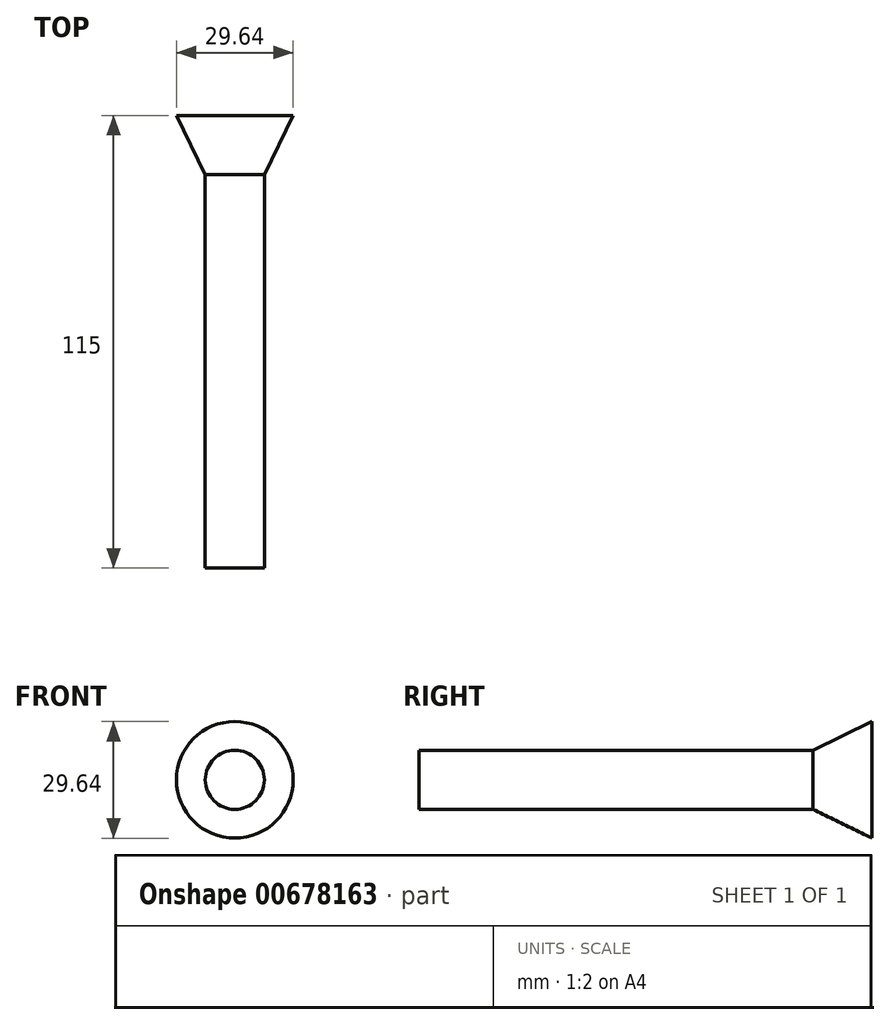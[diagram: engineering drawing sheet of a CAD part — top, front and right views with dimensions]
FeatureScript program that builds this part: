
annotation { "Feature Type Name" : "Feature", "Feature Type Description" : "" }
export const myFeature = defineFeature(function(context is Context, id is Id, definition is map)
    precondition{}
    {
        {
            var Q0;
            Q0=qCreatedBy(makeId("Front.planeOp"),FACE);
            var sketch = newSketch(context, id + "F0", { "sketchPlane" : qUnion([Q0])});
            skCircle(sketch, "E0", {"center": v(0, 0) * mm, "radius": 7.5 * mm});
            skSolve(sketch);
        }
        {
            var Q0;
            Q0=makeQuery(id+"F0.imprint","IMPRINT",FACE,{"disambiguationData":[TD([[makeQuery(id+"F0.imprint","IMPRINT",EDGE,{"derivedFrom":sQuery(id+"F0.wireOp",EDGE,"E0")}),1.0]])]});
            extrude(context, id + "F1", {"entities" : qUnion([Q0]), "depth" : 100 * mm, "offsetDistance" : 25 * mm});
        }
        {
            var Q0;
            Q0=makeQuery(id+"F1.opExtrude","CAP_FACE",FACE,{"disambiguationData":[OSD([sQuery(id+"F0.wireOp",EDGE,"E0")])],"isStart":true});
            extrude(context, id + "F2", {"entities" : qUnion([Q0]), "operationType" : NewBodyOperationType.ADD, "depth" : 15 * mm, "offsetDistance" : 25 * mm, "hasDraft" : true, "draftAngle" : 26 * degree});
        }
    });
